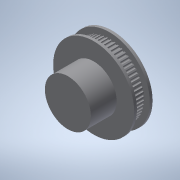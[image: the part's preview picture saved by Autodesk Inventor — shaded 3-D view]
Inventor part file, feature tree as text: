
AUTODESK INVENTOR PART (.ipt)
format: ipt  version: 2022 (Build 260153000, 153)  size: 264,704 bytes
history: native  units: mm
features: sketch x4, extrude x3, revolve x1, pattern_circular x1
ambient origin geometry x8: Origin, YZ Plane, XZ Plane, XY Plane, X Axis, Y Axis, Z Axis, Center Point
bodies: Solid1 (feature_tree)
feature tree (9):
  revolve  "Revolution1"  [1 undecoded]
  extrude  "Extrusion1"  Depth=18.95mm
  pattern_circular  "Circular Pattern1"  [2 undecoded]
  extrude  "Extrusion2"  Depth=10.0mm TaperAngle=0.0deg
  extrude  "Extrusion3"  Depth=8.0mm TaperAngle=360.0deg
  sketch  "Sketch1"  dims[d0=4.0mm d1=7.0mm]
  sketch  "Sketch2"  dims[d4=1.5mm d6=18.95mm]
  sketch  "Sketch3"  dims[d7=90.0deg]
  sketch  "Sketch4"  dims[d8=1.3mm d9=18.85mm d10=10.0mm d11=0.0mm d12=600.0mm d13=360.0deg d15=22.0mm d16=6.0mm d17=12.5mm d18=7.5mm d19=16.0mm d20=0.0mm d21=0.0mm d22=8.0mm d23=0.0mm]
note: 3 required parameter values undecoded (feature->parameter linkage not recoverable at this tier; creation-order binding heuristic only, values carry confidence <= 0.55)